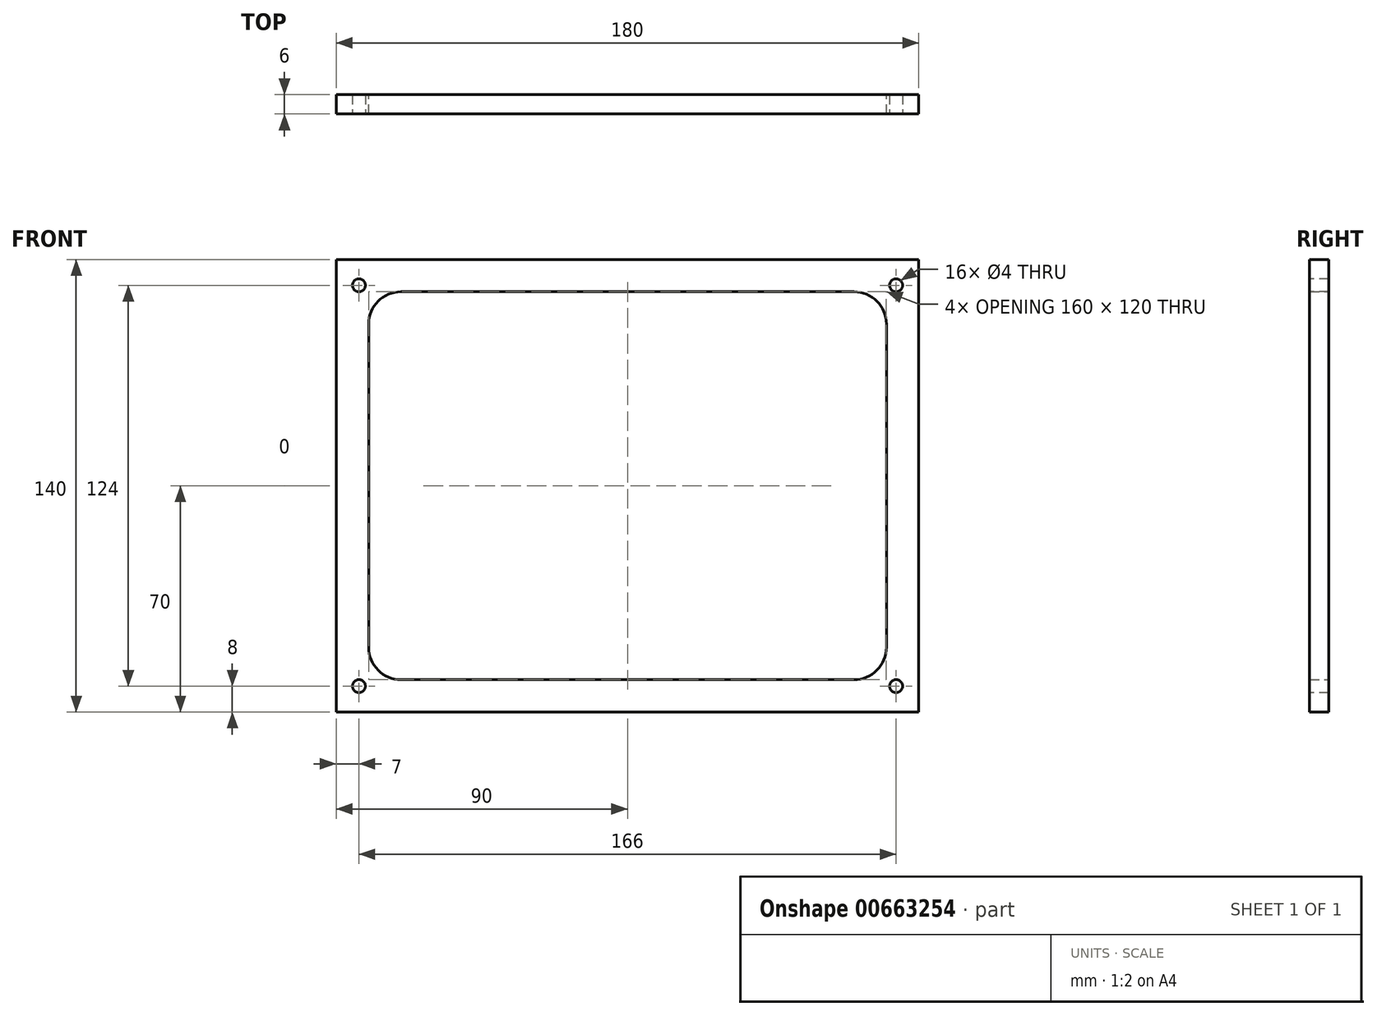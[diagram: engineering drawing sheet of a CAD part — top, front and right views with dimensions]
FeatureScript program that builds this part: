
annotation { "Feature Type Name" : "Feature", "Feature Type Description" : "" }
export const myFeature = defineFeature(function(context is Context, id is Id, definition is map)
    precondition{}
    {
        {
            var Q0;
            Q0=qCreatedBy(makeId("Front.planeOp"),FACE);
            var sketch = newSketch(context, id + "F0", { "sketchPlane" : qUnion([Q0])});
            skLineSegment(sketch, "E0.bottom", {"start": v(-90, -70) * mm, "end": v(90, -70) * mm});
            skLineSegment(sketch, "E0.top", {"start": v(-90, 70) * mm, "end": v(90, 70) * mm});
            skLineSegment(sketch, "E0.left", {"start": v(-90, -70) * mm, "end": v(-90, 70) * mm});
            skLineSegment(sketch, "E0.right", {"start": v(90, -70) * mm, "end": v(90, 70) * mm});
            skPoint(sketch, "E0.middle", {"position": v(0, 0) * mm});
            skLineSegment(sketch, "E1.0", {"start": v(-70, 60) * mm, "end": v(70, 60) * mm});
            skLineSegment(sketch, "E2.0", {"start": v(-80, -50) * mm, "end": v(-80, 50) * mm});
            skLineSegment(sketch, "E3.0", {"start": v(-70, -60) * mm, "end": v(70, -60) * mm});
            skLineSegment(sketch, "E4.0", {"start": v(80, -50) * mm, "end": v(80, 50) * mm});
            skPoint(sketch, "E5.visualSharp", {"position": v(-80, 60) * mm});
            skArc(sketch, "E5.filletArc", {"start": v(-70, 60) * mm, "mid": v(-77.07, 57.07) * mm, "end": v(-80, 50) * mm});
            skPoint(sketch, "E6.visualSharp", {"position": v(80, 60) * mm});
            skArc(sketch, "E6.filletArc", {"start": v(80, 50) * mm, "mid": v(77.07, 57.07) * mm, "end": v(70, 60) * mm});
            skPoint(sketch, "E7.visualSharp", {"position": v(80, -60) * mm});
            skArc(sketch, "E7.filletArc", {"start": v(70, -60) * mm, "mid": v(77.07, -57.07) * mm, "end": v(80, -50) * mm});
            skPoint(sketch, "E8.visualSharp", {"position": v(-80, -60) * mm});
            skArc(sketch, "E8.filletArc", {"start": v(-80, -50) * mm, "mid": v(-77.07, -57.07) * mm, "end": v(-70, -60) * mm});
            skLineSegment(sketch, "E9", {"start": v(0, 0) * mm, "end": v(0, 101.48) * mm});
            skLineSegment(sketch, "E10", {"start": v(0, 0) * mm, "end": v(117.35, 0) * mm});
            skPoint(sketch, "E10.endSnap0", {"position": v(90, 0) * mm});
            skSolve(sketch);
        }
        {
            var Q0;
            Q0 = qSketchRegion(id + "F0", true);
            extrude(context, id + "F1", {"entities" : qUnion([Q0]), "depth" : 6 * mm, "offsetDistance" : 25 * mm});
        }
        {
            var Q0;
            Q0=makeQuery(id+"F1.opExtrude","CAP_FACE",FACE,{"disambiguationData":[OSD([sQuery(id+"F0.wireOp",EDGE,"E0.bottom"),sQuery(id+"F0.wireOp",EDGE,"E0.top"),sQuery(id+"F0.wireOp",EDGE,"E0.left"),sQuery(id+"F0.wireOp",EDGE,"E0.right"),sQuery(id+"F0.wireOp",EDGE,"E1.0"),sQuery(id+"F0.wireOp",EDGE,"E2.0"),sQuery(id+"F0.wireOp",EDGE,"E3.0"),sQuery(id+"F0.wireOp",EDGE,"E4.0"),sQuery(id+"F0.wireOp",EDGE,"E5.filletArc"),sQuery(id+"F0.wireOp",EDGE,"E6.filletArc"),sQuery(id+"F0.wireOp",EDGE,"E7.filletArc"),sQuery(id+"F0.wireOp",EDGE,"E8.filletArc")])],"isStart":false});
            var sketch = newSketch(context, id + "F2", { "sketchPlane" : qUnion([Q0])});
            skCircle(sketch, "E11", {"center": v(-83, 62) * mm, "radius": 2 * mm});
            skPoint(sketch, "E12.endSnap0", {"position": v(90, 0) * mm});
            skLineSegment(sketch, "E13", {"start": v(0, 0) * mm, "end": v(-115.8, 0) * mm});
            skLineSegment(sketch, "E14", {"start": v(0, 0) * mm, "end": v(0, 81.19) * mm});
            skCircle(sketch, "E15.MirrorC", {"center": v(-83, -62) * mm, "radius": 2 * mm});
            skCircle(sketch, "E16.MirrorC", {"center": v(83, -62) * mm, "radius": 2 * mm});
            skCircle(sketch, "E17.MirrorC", {"center": v(83, 62) * mm, "radius": 2 * mm});
            skSolve(sketch);
        }
        {
            var Q0;
            Q0 = qSketchRegion(id + "F2", true);
            extrude(context, id + "F3", {"entities" : qUnion([Q0]), "operationType" : NewBodyOperationType.REMOVE, "oppositeDirection" : true, "depth" : 25 * mm, "offsetDistance" : 25 * mm});
        }
    });
